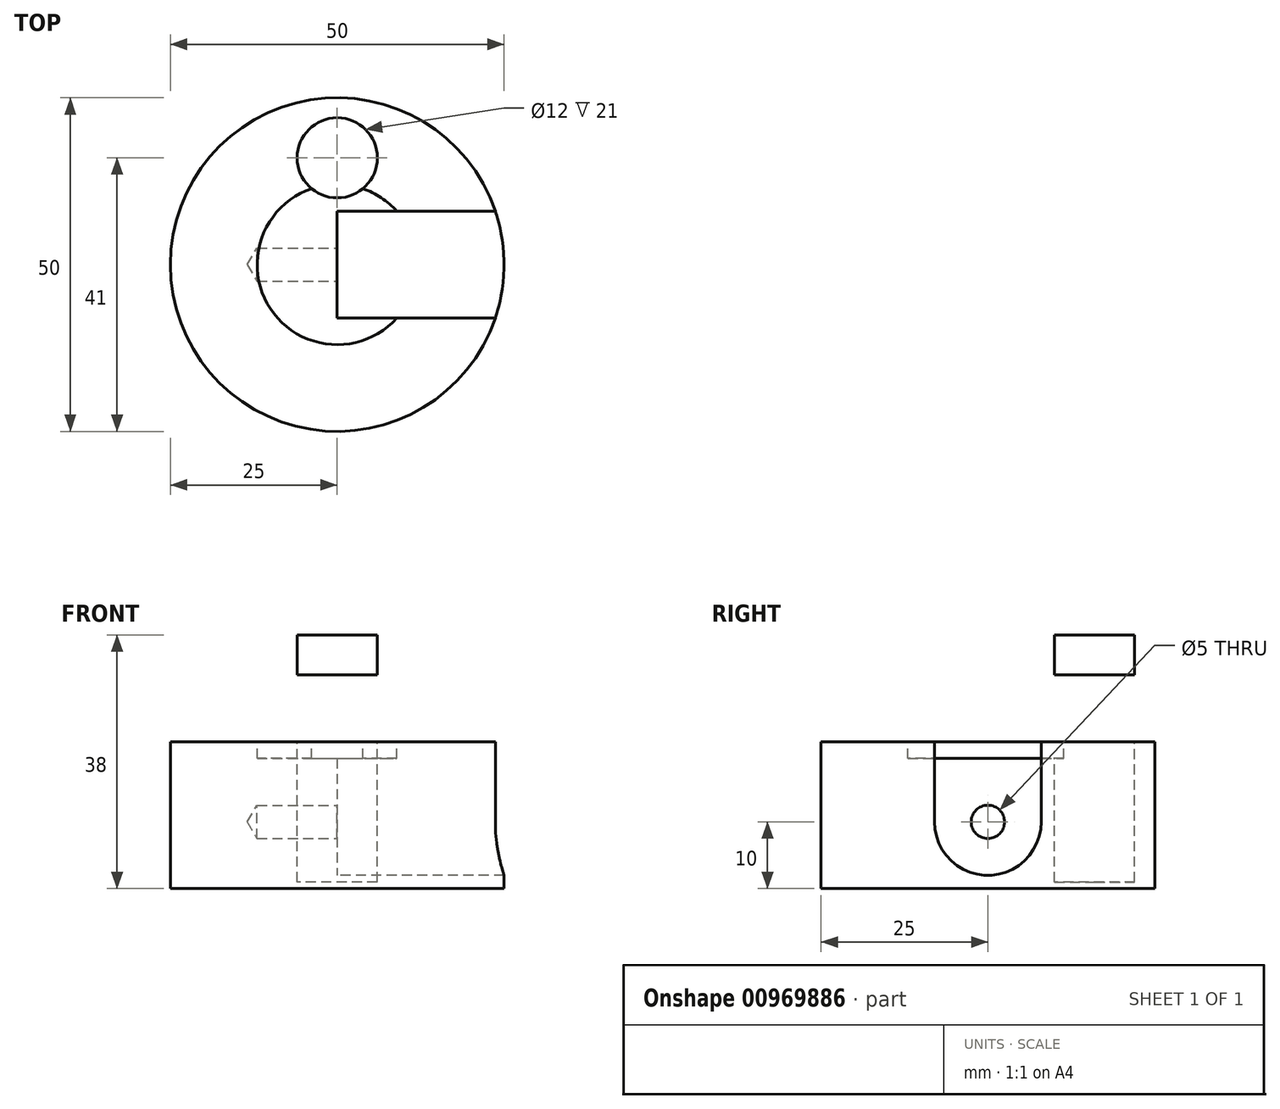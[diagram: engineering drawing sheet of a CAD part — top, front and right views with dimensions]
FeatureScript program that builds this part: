
annotation { "Feature Type Name" : "Feature", "Feature Type Description" : "" }
export const myFeature = defineFeature(function(context is Context, id is Id, definition is map)
    precondition{}
    {
        {
            var Q0;
            Q0=qCreatedBy(makeId("Top.planeOp"),FACE);
            var sketch = newSketch(context, id + "F0", { "sketchPlane" : qUnion([Q0])});
            skCircle(sketch, "E0", {"center": v(0, 0) * mm, "radius": 25 * mm});
            skSolve(sketch);
        }
        {
            var Q0;
            Q0 = qSketchRegion(id + "F0", true);
            extrude(context, id + "F1", {"entities" : qUnion([Q0]), "depth" : 22 * mm, "offsetDistance" : 25 * mm});
        }
        {
            var Q0;
            Q0=makeQuery(id+"F1.opExtrude","CAP_FACE",FACE,{"disambiguationData":[OSD([sQuery(id+"F0.wireOp",EDGE,"E0")])],"isStart":false});
            var sketch = newSketch(context, id + "F2", { "sketchPlane" : qUnion([Q0])});
            skPoint(sketch, "E1", {"position": v(0, 0) * mm});
            skSolve(sketch);
        }
        {
            var Q0;
            Q0=qCreatedBy(makeId("Right.planeOp"),FACE);
            var sketch = newSketch(context, id + "F3", { "sketchPlane" : qUnion([Q0])});
            skLineSegment(sketch, "E2.bottom", {"start": v(8, 42) * mm, "end": v(-8, 42) * mm});
            skLineSegment(sketch, "E2.top", {"start": v(0, 2) * mm, "end": v(0, 2) * mm});
            skLineSegment(sketch, "E2.left", {"start": v(8, 42) * mm, "end": v(8, 10) * mm});
            skLineSegment(sketch, "E2.right", {"start": v(-8, 42) * mm, "end": v(-8, 10) * mm});
            skPoint(sketch, "E2.middle", {"position": v(0, 22) * mm});
            skPoint(sketch, "E3.visualSharp", {"position": v(-8, 2) * mm});
            skArc(sketch, "E3.filletArc", {"start": v(-8, 10) * mm, "mid": v(-5.66, 4.34) * mm, "end": v(0, 2) * mm});
            skPoint(sketch, "E4.visualSharp", {"position": v(8, 2) * mm});
            skArc(sketch, "E4.filletArc", {"start": v(0, 2) * mm, "mid": v(5.66, 4.34) * mm, "end": v(8, 10) * mm});
            skSolve(sketch);
        }
        {
            var Q0;
            Q0 = qSketchRegion(id + "F3", true);
            var Q1;
            Q1=makeQuery(id+"F1.opExtrude","SWEPT_FACE",FACE,{"disambiguationData":[OSD([sQuery(id+"F0.wireOp",EDGE,"E0")])]});
            extrude(context, id + "F4", {"entities" : qUnion([Q0]), "operationType" : NewBodyOperationType.REMOVE, "endBound" : BoundingType.UP_TO_SURFACE, "depth" : 25 * mm, "endBoundEntityFace" : qUnion([Q1]), "offsetDistance" : 25 * mm, "hasSecondDirection" : true, "secondDirectionOppositeDirection" : true, "secondDirectionDepth" : 1 / 203.2 * mm});
        }
        {
            var Q0;
            Q0=makeQuery(id+"F2.imprint","IMPRINT",FACE,{"disambiguationData":[TD([[makeQuery(id+"F2.imprint","IMPRINT",EDGE,{"derivedFrom":makeQuery(id+"F1.opExtrude","CAP_EDGE",EDGE,{"disambiguationData":[OSD([sQuery(id+"F0.wireOp",EDGE,"E0")])],"isStart":false})}),1.0]])]});
            var sketch = newSketch(context, id + "F5", { "sketchPlane" : qUnion([Q0])});
            skCircle(sketch, "E5", {"center": v(0, 16) * mm, "radius": 6 * mm});
            skSolve(sketch);
        }
        {
            var Q0;
            Q0 = qSketchRegion(id + "F5", true);
            extrude(context, id + "F6", {"entities" : qUnion([Q0]), "operationType" : NewBodyOperationType.REMOVE, "oppositeDirection" : true, "depth" : 21 * mm, "offsetDistance" : 25 * mm});
        }
        {
            var Q0;
            Q0=makeQuery(id+"F4.boolean.opBoolean","COPY",FACE,{"derivedFrom":makeQuery(id+"F4.opExtrude","CAP_FACE",FACE,{"disambiguationData":[OSD([sQuery(id+"F3.wireOp",EDGE,"E2.bottom"),sQuery(id+"F3.wireOp",EDGE,"E2.left"),sQuery(id+"F3.wireOp",EDGE,"E2.right"),sQuery(id+"F3.wireOp",EDGE,"E3.filletArc"),sQuery(id+"F3.wireOp",EDGE,"E4.filletArc")])],"isStart":true})});
            var sketch = newSketch(context, id + "F7", { "sketchPlane" : qUnion([Q0])});
            skPoint(sketch, "E6", {"position": v(0, 10) * mm});
            skSolve(sketch);
        }
        {
            var Q0;
            Q0=sQuery(id+"F7.wireOp",VERTEX,"E6");
            var Q1;
            Q1=makeQuery(id+"F1.opExtrude","SWEPT_BODY",BODY,{"disambiguationData":[OSD([sQuery(id+"F0.wireOp",EDGE,"E0")])]});
            hole(context, id + "F8", {"style" : HoleStyle.SIMPLE, "endStyle" : HoleEndStyle.BLIND, "standardTappedOrClearance" : lookupTablePath({ "standard" : "ISO", "engagement" : "75%", "pitch" : "1 mm", "size" : "M6", "type" : "Tapped" }), "standardBlindInLast" : lookupTablePath({ "standard" : "ISO", "fit" : "Normal", "engagement" : "75%", "pitch" : "1 mm", "size" : "M6", "type" : "Clearance & tapped" }), "holeDiameter" : 5 * mm, "majorDiameter" : 6 * mm, "showTappedDepth" : true, "holeDepth" : 12 * mm, "tappedDepth" : 9 * mm, "tapClearance" : 3, "locations" : qUnion([Q0]), "scope" : qUnion([Q1])});
        }
        {
            var Q0;
            Q0=makeQuery(id+"F1.opExtrude","CAP_FACE",FACE,{"disambiguationData":[OSD([sQuery(id+"F0.wireOp",EDGE,"E0")])],"isStart":false});
            var sketch = newSketch(context, id + "F9", { "sketchPlane" : qUnion([Q0])});
            skCircle(sketch, "E7", {"center": v(0, 0) * mm, "radius": 12 * mm});
            skSolve(sketch);
        }
        {
            var Q0;
            Q0 = qSketchRegion(id + "F9", true);
            extrude(context, id + "F10", {"entities" : qUnion([Q0]), "operationType" : NewBodyOperationType.REMOVE, "oppositeDirection" : true, "depth" : 2.5 * mm, "offsetDistance" : 25 * mm});
        }
        {
            var Q0;
            Q0=makeQuery(id+"F1.opExtrude","CAP_FACE",FACE,{"disambiguationData":[OSD([sQuery(id+"F0.wireOp",EDGE,"E0")])],"isStart":false});
            cPlane(context, id + "F11", {"entities" : qUnion([Q0]), "cplaneType" : CPlaneType.OFFSET, "offset" : 10 * mm, "width" : 150 * mm, "height" : 150 * mm});
        }
        {
            var Q0;
            Q0=qCreatedBy(id+"F11.planeOp",FACE);
            var sketch = newSketch(context, id + "F12", { "sketchPlane" : qUnion([Q0])});
            skCircle(sketch, "E8", {"center": v(0, 16) * mm, "radius": 6 * mm});
            skSolve(sketch);
        }
        {
            var Q0;
            Q0 = qSketchRegion(id + "F12", true);
            extrude(context, id + "F13", {"entities" : qUnion([Q0]), "depth" : 6 * mm, "offsetDistance" : 25 * mm});
        }
    });
